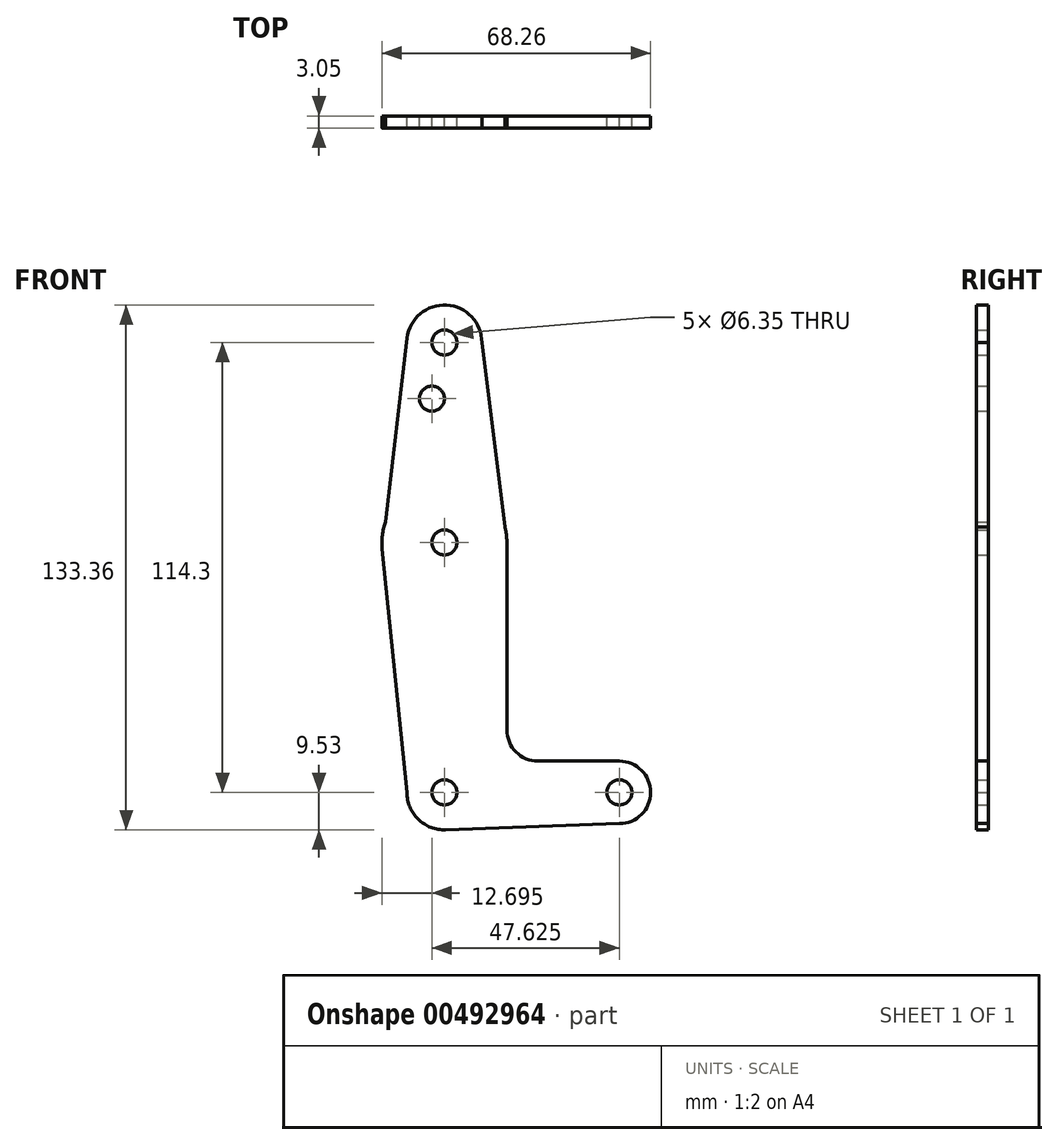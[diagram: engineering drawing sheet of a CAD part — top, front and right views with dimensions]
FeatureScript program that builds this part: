
annotation { "Feature Type Name" : "Feature", "Feature Type Description" : "" }
export const myFeature = defineFeature(function(context is Context, id is Id, definition is map)
    precondition{}
    {
        {
            var Q0;
            Q0=qCreatedBy(makeId("Front.planeOp"),FACE);
            var sketch = newSketch(context, id + "F0", { "sketchPlane" : qUnion([Q0])});
            skLineSegment(sketch, "E0", {"start": v(0, 0) * mm, "end": v(44.45, 0) * mm, "construction": true});
            skCircle(sketch, "E1", {"center": v(0, 114.3) * mm, "radius": 9.53 * mm});
            skCircle(sketch, "E2", {"center": v(0, 0) * mm, "radius": 9.53 * mm});
            skCircle(sketch, "E3", {"center": v(44.45, 0) * mm, "radius": 7.94 * mm});
            skLineSegment(sketch, "E4", {"start": v(0, 0) * mm, "end": v(0, 114.3) * mm, "construction": true});
            skCircle(sketch, "E5", {"center": v(0, 63.5) * mm, "radius": 15.88 * mm});
            skLineSegment(sketch, "E6", {"start": v(-9.53, 0) * mm, "end": v(-15.8, 61.9) * mm});
            skLineSegment(sketch, "E7", {"start": v(-15.8, 61.9) * mm, "end": v(-9.46, 115.42) * mm});
            skLineSegment(sketch, "E8", {"start": v(9.53, 114.3) * mm, "end": v(15.88, 63.5) * mm});
            skLineSegment(sketch, "E9", {"start": v(15.88, 63.5) * mm, "end": v(15.88, 15.89) * mm});
            skLineSegment(sketch, "E10", {"start": v(44.45, -7.94) * mm, "end": v(0, -9.53) * mm});
            skLineSegment(sketch, "E11", {"start": v(23.83, 7.94) * mm, "end": v(44.45, 7.94) * mm});
            skCircle(sketch, "E12", {"center": v(-3.18, 100.03) * mm, "radius": 3.18 * mm});
            skCircle(sketch, "E13", {"center": v(0, 114.3) * mm, "radius": 3.18 * mm});
            skCircle(sketch, "E14", {"center": v(0, 63.5) * mm, "radius": 3.18 * mm});
            skCircle(sketch, "E15", {"center": v(0, 0) * mm, "radius": 3.18 * mm});
            skCircle(sketch, "E16", {"center": v(44.45, 0) * mm, "radius": 3.18 * mm});
            skPoint(sketch, "E17.newPointA", {"position": v(15.88, 0) * mm});
            skArc(sketch, "E17.filletArc", {"start": v(15.88, 15.89) * mm, "mid": v(18.2, 10.27) * mm, "end": v(23.83, 7.94) * mm});
            skSolve(sketch);
        }
        {
            var Q0;
            Q0 = qSketchRegion(id + "F0", true);
            extrude(context, id + "F1", {"entities" : qUnion([Q0]), "depth" : 3.05 * mm});
        }
    });
